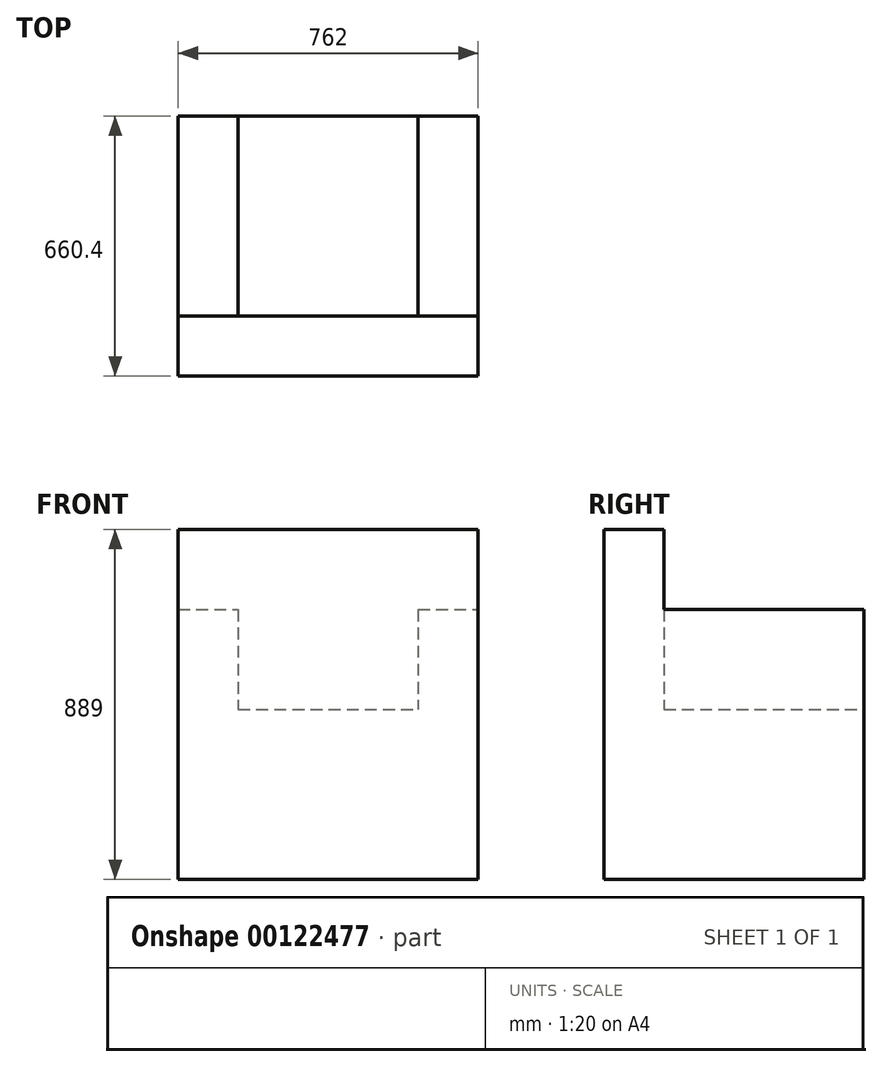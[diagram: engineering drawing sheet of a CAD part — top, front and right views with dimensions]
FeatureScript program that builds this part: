
annotation { "Feature Type Name" : "Feature", "Feature Type Description" : "" }
export const myFeature = defineFeature(function(context is Context, id is Id, definition is map)
    precondition{}
    {
        {
            var Q0;
            Q0=qCreatedBy(makeId("Top.planeOp"),FACE);
            var sketch = newSketch(context, id + "F0", { "sketchPlane" : qUnion([Q0])});
            skLineSegment(sketch, "E0.bottom", {"start": v(0, 0) * mm, "end": v(762, 0) * mm});
            skLineSegment(sketch, "E0.top", {"start": v(0, -660.4) * mm, "end": v(762, -660.4) * mm});
            skLineSegment(sketch, "E0.left", {"start": v(0, 0) * mm, "end": v(0, -660.4) * mm});
            skLineSegment(sketch, "E0.right", {"start": v(762, 0) * mm, "end": v(762, -660.4) * mm});
            skSolve(sketch);
        }
        {
            var Q0;
            Q0=qSketchRegion(id+"F0",true);
            extrude(context, id + "F1", {"entities" : qUnion([Q0]), "depth" : 431.8 * mm});
        }
        {
            var Q0;
            Q0=makeQuery(id+"F1.opExtrude","CAP_FACE",FACE,{"disambiguationData":[OSD([sQuery(id+"F0.wireOp",EDGE,"E0.bottom"),sQuery(id+"F0.wireOp",EDGE,"E0.top"),sQuery(id+"F0.wireOp",EDGE,"E0.left"),sQuery(id+"F0.wireOp",EDGE,"E0.right")])],"isStart":false});
            var sketch = newSketch(context, id + "F2", { "sketchPlane" : qUnion([Q0])});
            skLineSegment(sketch, "E1.bottom", {"start": v(0, -660.4) * mm, "end": v(762, -660.4) * mm});
            skLineSegment(sketch, "E1.top", {"start": v(0, -508) * mm, "end": v(762, -508) * mm});
            skLineSegment(sketch, "E1.left", {"start": v(0, -660.4) * mm, "end": v(0, -508) * mm});
            skLineSegment(sketch, "E1.right", {"start": v(762, -660.4) * mm, "end": v(762, -508) * mm});
            skSolve(sketch);
        }
        {
            var Q0;
            Q0=qSketchRegion(id+"F2",true);
            extrude(context, id + "F3", {"entities" : qUnion([Q0]), "operationType" : NewBodyOperationType.ADD, "depth" : 457.2 * mm});
        }
        {
            var Q0;
            Q0=makeQuery(id+"F1.opExtrude","CAP_FACE",FACE,{"disambiguationData":[OSD([sQuery(id+"F0.wireOp",EDGE,"E0.bottom"),sQuery(id+"F0.wireOp",EDGE,"E0.top"),sQuery(id+"F0.wireOp",EDGE,"E0.left"),sQuery(id+"F0.wireOp",EDGE,"E0.right")])],"isStart":false});
            var sketch = newSketch(context, id + "F4", { "sketchPlane" : qUnion([Q0])});
            skLineSegment(sketch, "E2.bottom", {"start": v(0, -508) * mm, "end": v(152.4, -508) * mm});
            skLineSegment(sketch, "E2.top", {"start": v(0, 0) * mm, "end": v(152.4, 0) * mm});
            skLineSegment(sketch, "E2.left", {"start": v(0, -508) * mm, "end": v(0, 0) * mm});
            skLineSegment(sketch, "E2.right", {"start": v(152.4, -508) * mm, "end": v(152.4, 0) * mm});
            skSolve(sketch);
        }
        {
            var Q0;
            Q0=qSketchRegion(id+"F4",true);
            extrude(context, id + "F5", {"entities" : qUnion([Q0]), "operationType" : NewBodyOperationType.ADD, "depth" : 254 * mm});
        }
        {
            var Q0;
            Q0=makeQuery(id+"F1.opExtrude","CAP_FACE",FACE,{"disambiguationData":[OSD([sQuery(id+"F0.wireOp",EDGE,"E0.bottom"),sQuery(id+"F0.wireOp",EDGE,"E0.top"),sQuery(id+"F0.wireOp",EDGE,"E0.left"),sQuery(id+"F0.wireOp",EDGE,"E0.right")])],"isStart":false});
            var sketch = newSketch(context, id + "F6", { "sketchPlane" : qUnion([Q0])});
            skLineSegment(sketch, "E3.bottom", {"start": v(762, -508) * mm, "end": v(609.6, -508) * mm});
            skLineSegment(sketch, "E3.top", {"start": v(762, 0) * mm, "end": v(609.6, 0) * mm});
            skLineSegment(sketch, "E3.left", {"start": v(762, -508) * mm, "end": v(762, 0) * mm});
            skLineSegment(sketch, "E3.right", {"start": v(609.6, -508) * mm, "end": v(609.6, 0) * mm});
            skSolve(sketch);
        }
        {
            var Q0;
            Q0=qSketchRegion(id+"F6",true);
            extrude(context, id + "F7", {"entities" : qUnion([Q0]), "operationType" : NewBodyOperationType.ADD, "depth" : 254 * mm});
        }
    });
